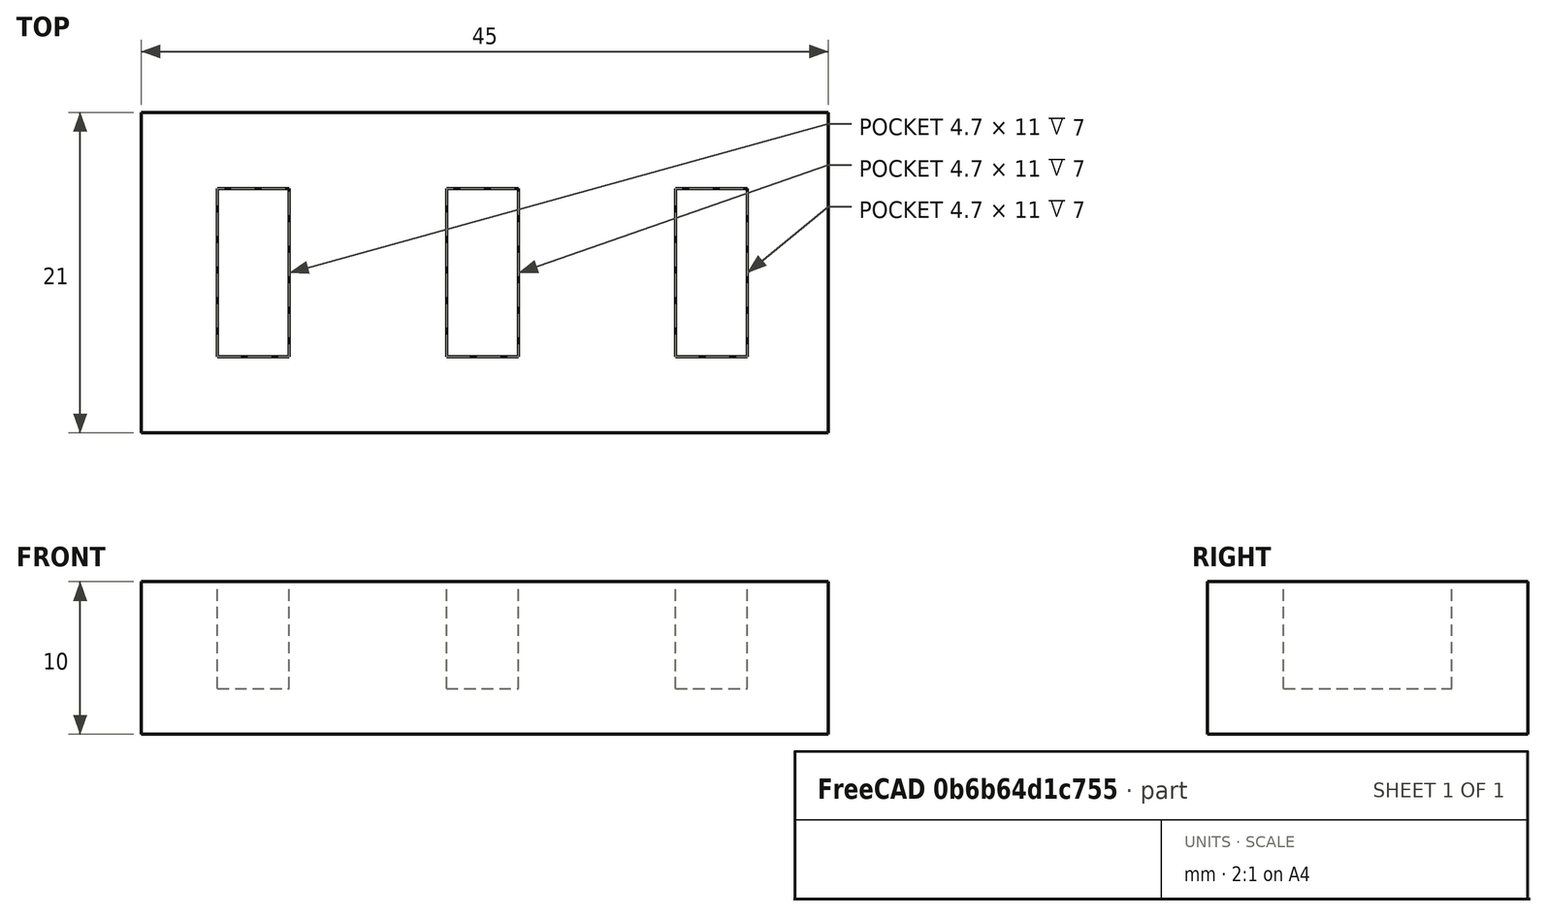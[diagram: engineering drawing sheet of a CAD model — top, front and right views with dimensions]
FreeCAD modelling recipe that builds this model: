
FCSTD DOCUMENT  (FreeCAD 1.0R39319 (Git))
Label: ojt1_t08_p01_usb_flash
License: All rights reserved
LicenseURL: https://en.wikipedia.org/wiki/All_rights_reserved
objects: Part::Box×4, Part::MultiFuse×1, Part::Cut×1
note: 6 computed .brp shape members not serialized (recipe doc carries the construction recipe); baked Part::Feature solids carry a one-line shape summary decoded from their .brp

FEATURE [Part::Box] Box  label="Ranura_1"
  AttacherType = Attacher::AttachEngine3D
  Height = 12
  Length = 4.7
  Width = 11
FEATURE [Part::Box] Box001  label="Ranura_002"
  AttacherType = Attacher::AttachEngine3D
  Height = 12
  Length = 4.7
  Placement = pos=(15,0,0) rot=(0,0,1;0rad)
  Width = 11
FEATURE [Part::Box] Box002  label="Ranura_003"
  AttacherType = Attacher::AttachEngine3D
  Height = 12
  Length = 4.7
  Placement = pos=(30,0,0) rot=(0,0,1;0rad)
  Width = 11
FEATURE [Part::MultiFuse] Fusion  label="Ranuras"
  Placement = pos=(0,0,3) rot=(0,0,1;0rad)
  Refine = true
  Shapes = -> [Box002,Box001,Box]
FEATURE [Part::Box] Box003  label="Base"
  AttacherType = Attacher::AttachEngine3D
  Height = 10
  Length = 45
  Placement = pos=(-5,-5,0) rot=(0,0,1;0rad)
  Width = 21
FEATURE [Part::Cut] Cut  label="Porta-Pendrives"
  Base = -> Box003
  Refine = true
  Tool = -> Fusion
